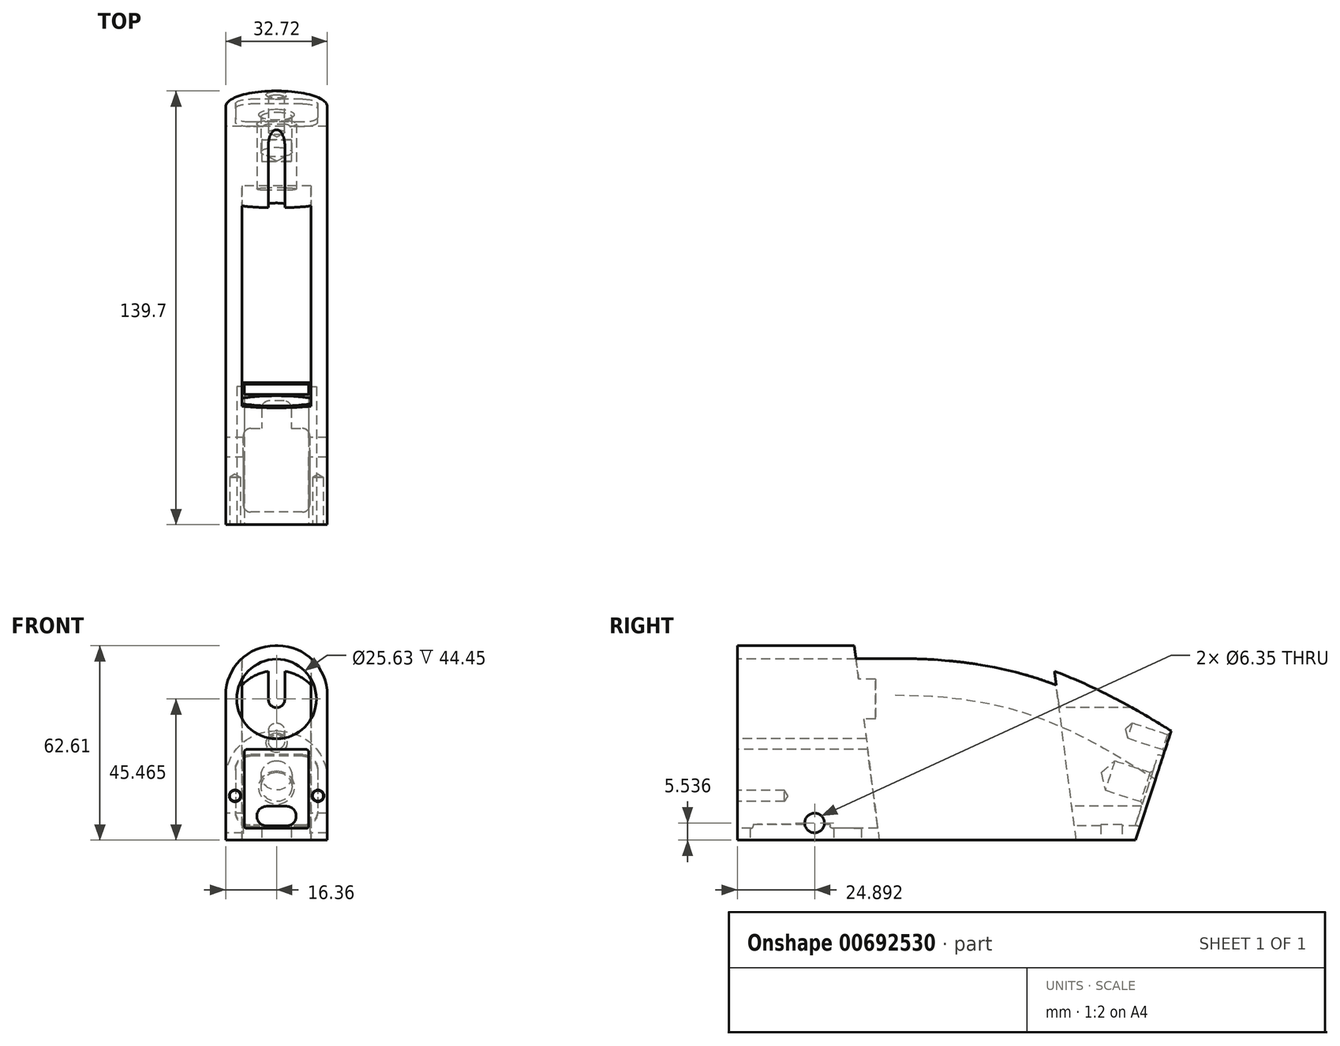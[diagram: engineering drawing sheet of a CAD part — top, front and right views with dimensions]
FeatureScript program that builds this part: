
annotation { "Feature Type Name" : "Feature", "Feature Type Description" : "" }
export const myFeature = defineFeature(function(context is Context, id is Id, definition is map)
    precondition{}
    {
        {
            var Q0;
            Q0=qCreatedBy(makeId("Right.planeOp"),FACE);
            var sketch = newSketch(context, id + "F0", { "sketchPlane" : qUnion([Q0])});
            skLineSegment(sketch, "E0.bottom", {"start": v(0, 0) * mm, "end": v(50.8, 0) * mm});
            skLineSegment(sketch, "E0.top", {"start": v(0, -62.61) * mm, "end": v(128.27, -62.61) * mm});
            skLineSegment(sketch, "E0.left", {"start": v(0, 0) * mm, "end": v(0, -62.61) * mm});
            skCircle(sketch, "E1", {"center": v(24.9, -57.07) * mm, "radius": 3.18 * mm});
            skLineSegment(sketch, "E2", {"start": v(128.27, -62.61) * mm, "end": v(139.7, -27.43) * mm});
            skFitSpline(sketch, "E3", {"points": [v(139.7, -27.43) * mm, v(50.8, 0) * mm], "startDerivative": vector(-81.05, 50.52) * mm, "endDerivative": vector(-120.57, 0) * mm});
            skSolve(sketch);
        }
        {
            var Q0;
            Q0 = qSketchRegion(id + "F0", true);
            extrude(context, id + "F1", {"entities" : qUnion([Q0]), "endBound" : BoundingType.SYMMETRIC, "depth" : 32.72 * mm, "offsetDistance" : 25.4 * mm});
        }
        {
            var Q0;
            Q0=qCreatedBy(makeId("Right.planeOp"),FACE);
            var sketch = newSketch(context, id + "F2", { "sketchPlane" : qUnion([Q0])});
            skLineSegment(sketch, "E4", {"start": v(36.1, 12.1) * mm, "end": v(45.72, -62.61) * mm});
            skLineSegment(sketch, "E5", {"start": v(45.72, -62.61) * mm, "end": v(109.1, -62.61) * mm});
            skLineSegment(sketch, "E6", {"start": v(109.1, -62.61) * mm, "end": v(98.46, 20.11) * mm});
            skLineSegment(sketch, "E7", {"start": v(98.46, 20.11) * mm, "end": v(36.1, 12.1) * mm});
            skSolve(sketch);
        }
        {
            var Q0;
            Q0=makeQuery(id+"F2.imprint","IMPRINT",FACE,{"disambiguationData":[TD([[makeQuery(id+"F2.imprint","IMPRINT",EDGE,{"derivedFrom":sQuery(id+"F2.wireOp",EDGE,"E4")}),1.0]])]});
            extrude(context, id + "F3", {"entities" : qUnion([Q0]), "operationType" : NewBodyOperationType.REMOVE, "endBound" : BoundingType.SYMMETRIC, "depth" : 22.22 * mm, "offsetDistance" : 25.4 * mm});
        }
        {
            var Q0;
            Q0=makeQuery(id+"F1.opExtrude","SWEPT_FACE",FACE,{"disambiguationData":[OSD([sQuery(id+"F0.wireOp",EDGE,"E2")])]});
            var sketch = newSketch(context, id + "F4", { "sketchPlane" : qUnion([Q0])});
            skLineSegment(sketch, "E8.bottom", {"start": v(-8.46, 8.54) * mm, "end": v(8.46, 8.54) * mm});
            skLineSegment(sketch, "E8.top", {"start": v(-8.46, -15.34) * mm, "end": v(8.46, -15.34) * mm});
            skLineSegment(sketch, "E8.left", {"start": v(-13.2, 3.79) * mm, "end": v(-13.2, -10.59) * mm});
            skLineSegment(sketch, "E8.right", {"start": v(13.2, 3.79) * mm, "end": v(13.2, -10.59) * mm});
            skPoint(sketch, "E9.visualSharp", {"position": v(-13.2, 8.54) * mm});
            skArc(sketch, "E9.filletArc", {"start": v(-8.46, 8.54) * mm, "mid": v(-11.82, 7.15) * mm, "end": v(-13.2, 3.79) * mm});
            skPoint(sketch, "E10.visualSharp", {"position": v(13.2, 8.54) * mm});
            skArc(sketch, "E10.filletArc", {"start": v(13.2, 3.79) * mm, "mid": v(11.82, 7.15) * mm, "end": v(8.46, 8.54) * mm});
            skPoint(sketch, "E11.visualSharp", {"position": v(13.2, -15.34) * mm});
            skArc(sketch, "E11.filletArc", {"start": v(8.46, -15.34) * mm, "mid": v(11.82, -13.95) * mm, "end": v(13.2, -10.59) * mm});
            skPoint(sketch, "E12.visualSharp", {"position": v(-13.2, -15.34) * mm});
            skArc(sketch, "E12.filletArc", {"start": v(-13.2, -10.59) * mm, "mid": v(-11.82, -13.95) * mm, "end": v(-8.46, -15.34) * mm});
            skCircle(sketch, "E13", {"center": v(0, -2.64) * mm, "radius": 5.55 * mm});
            skCircle(sketch, "E14", {"center": v(0, 13.11) * mm, "radius": 3.18 * mm});
            skSolve(sketch);
        }
        {
            var Q0;
            Q0=makeQuery(id+"F4.imprint","IMPRINT",FACE,{"disambiguationData":[TD([[makeQuery(id+"F4.imprint","IMPRINT",EDGE,{"derivedFrom":sQuery(id+"F4.wireOp",EDGE,"E8.bottom")}),-1.0]])]});
            extrude(context, id + "F5", {"entities" : qUnion([Q0]), "operationType" : NewBodyOperationType.REMOVE, "oppositeDirection" : true, "depth" : 1.6 * mm, "offsetDistance" : 25.4 * mm});
        }
        {
            var Q0;
            Q0=sQuery(id+"F4.wireOp",VERTEX,"E14.center");
            var Q1;
            Q1=makeQuery(id+"F1.opExtrude","SWEPT_BODY",BODY,{"disambiguationData":[OSD([sQuery(id+"F0.wireOp",EDGE,"E0.bottom"),sQuery(id+"F0.wireOp",EDGE,"E0.top"),sQuery(id+"F0.wireOp",EDGE,"E0.left"),sQuery(id+"F0.wireOp",EDGE,"E1"),sQuery(id+"F0.wireOp",EDGE,"E2"),sQuery(id+"F0.wireOp",EDGE,"E3")])]});
            hole(context, id + "F6", {"style" : HoleStyle.C_SINK, "endStyle" : HoleEndStyle.BLIND, "holeDiameter" : 5.1 * mm, "cSinkDiameter" : 6.73 * mm, "cSinkAngle" : 90 * degree, "majorDiameter" : 6.35 * mm, "holeDepth" : 12.7 * mm, "isTappedThrough" : true, "tappedDepth" : 12.7 * mm, "tapClearance" : 3, "locations" : qUnion([Q0]), "scope" : qUnion([Q1])});
        }
        {
            var Q0;
            Q0=sQuery(id+"F4.wireOp",VERTEX,"E13.center");
            var Q1;
            Q1=makeQuery(id+"F1.opExtrude","SWEPT_BODY",BODY,{"disambiguationData":[OSD([sQuery(id+"F0.wireOp",EDGE,"E0.bottom"),sQuery(id+"F0.wireOp",EDGE,"E0.top"),sQuery(id+"F0.wireOp",EDGE,"E0.left"),sQuery(id+"F0.wireOp",EDGE,"E1"),sQuery(id+"F0.wireOp",EDGE,"E2"),sQuery(id+"F0.wireOp",EDGE,"E3")])]});
            hole(context, id + "F7", {"style" : HoleStyle.C_SINK, "endStyle" : HoleEndStyle.BLIND, "holeDiameter" : 9.92 * mm, "cSinkDiameter" : 11.43 * mm, "cSinkAngle" : 90 * degree, "majorDiameter" : 6.35 * mm, "holeDepth" : 12.7 * mm, "isTappedThrough" : true, "tappedDepth" : 12.7 * mm, "tapClearance" : 3, "locations" : qUnion([Q0]), "scope" : qUnion([Q1])});
        }
        {
            var Q0;
            Q0=qCreatedBy(makeId("Front.planeOp"),FACE);
            var sketch = newSketch(context, id + "F8", { "sketchPlane" : qUnion([Q0])});
            skLineSegment(sketch, "E15.bottom", {"start": v(3.17, -58.04) * mm, "end": v(-3.17, -58.04) * mm});
            skLineSegment(sketch, "E15.top", {"start": v(3.17, -51.69) * mm, "end": v(-3.18, -51.69) * mm});
            skLineSegment(sketch, "E15.left", {"start": v(6.35, -54.86) * mm, "end": v(6.35, -54.86) * mm});
            skLineSegment(sketch, "E15.right", {"start": v(-6.35, -54.86) * mm, "end": v(-6.35, -54.86) * mm});
            skPoint(sketch, "E15.middle", {"position": v(0, -54.86) * mm});
            skPoint(sketch, "E16.visualSharp", {"position": v(-6.35, -51.69) * mm});
            skArc(sketch, "E16.filletArc", {"start": v(-3.18, -51.69) * mm, "mid": v(-5.42, -52.62) * mm, "end": v(-6.35, -54.86) * mm});
            skPoint(sketch, "E17.visualSharp", {"position": v(6.35, -51.69) * mm});
            skArc(sketch, "E17.filletArc", {"start": v(6.35, -54.86) * mm, "mid": v(5.42, -52.62) * mm, "end": v(3.17, -51.69) * mm});
            skPoint(sketch, "E18.visualSharp", {"position": v(6.35, -58.04) * mm});
            skArc(sketch, "E18.filletArc", {"start": v(3.17, -58.04) * mm, "mid": v(5.42, -57.1) * mm, "end": v(6.35, -54.86) * mm});
            skPoint(sketch, "E19.visualSharp", {"position": v(-6.35, -58.04) * mm});
            skArc(sketch, "E19.filletArc", {"start": v(-6.35, -54.86) * mm, "mid": v(-5.42, -57.1) * mm, "end": v(-3.17, -58.04) * mm});
            skSolve(sketch);
        }
        {
            var Q0;
            Q0=makeQuery(id+"F8.imprint","IMPRINT",FACE,{"disambiguationData":[TD([[makeQuery(id+"F8.imprint","IMPRINT",EDGE,{"derivedFrom":sQuery(id+"F8.wireOp",EDGE,"E15.bottom")}),-1.0]])]});
            extrude(context, id + "F9", {"entities" : qUnion([Q0]), "operationType" : NewBodyOperationType.REMOVE, "endBound" : BoundingType.THROUGH_ALL, "oppositeDirection" : true, "depth" : 25.4 * mm, "offsetDistance" : 25.4 * mm});
        }
        {
            var Q0;
            Q0=qCreatedBy(makeId("Front.planeOp"),FACE);
            var sketch = newSketch(context, id + "F10", { "sketchPlane" : qUnion([Q0])});
            skLineSegment(sketch, "E20.bottom", {"start": v(-9.59, -58.8) * mm, "end": v(9.59, -58.8) * mm});
            skLineSegment(sketch, "E20.top", {"start": v(-9.59, -33.4) * mm, "end": v(9.59, -33.4) * mm});
            skLineSegment(sketch, "E20.left", {"start": v(-10.35, -58.04) * mm, "end": v(-10.35, -34.16) * mm});
            skLineSegment(sketch, "E20.right", {"start": v(10.35, -58.04) * mm, "end": v(10.35, -34.16) * mm});
            skPoint(sketch, "E20.middle", {"position": v(0, -46.1) * mm});
            skPoint(sketch, "E21.visualSharp", {"position": v(-10.35, -33.4) * mm});
            skArc(sketch, "E21.filletArc", {"start": v(-9.59, -33.4) * mm, "mid": v(-10.13, -33.62) * mm, "end": v(-10.35, -34.16) * mm});
            skPoint(sketch, "E22.visualSharp", {"position": v(10.35, -33.4) * mm});
            skArc(sketch, "E22.filletArc", {"start": v(10.35, -34.16) * mm, "mid": v(10.13, -33.62) * mm, "end": v(9.59, -33.4) * mm});
            skPoint(sketch, "E23.visualSharp", {"position": v(10.35, -58.8) * mm});
            skArc(sketch, "E23.filletArc", {"start": v(9.59, -58.8) * mm, "mid": v(10.13, -58.58) * mm, "end": v(10.35, -58.04) * mm});
            skPoint(sketch, "E24.visualSharp", {"position": v(-10.35, -58.8) * mm});
            skArc(sketch, "E24.filletArc", {"start": v(-10.35, -58.04) * mm, "mid": v(-10.13, -58.58) * mm, "end": v(-9.59, -58.8) * mm});
            skSolve(sketch);
        }
        {
            var Q0;
            Q0 = qSketchRegion(id + "F10", true);
            extrude(context, id + "F11", {"entities" : qUnion([Q0]), "operationType" : NewBodyOperationType.REMOVE, "endBound" : BoundingType.UP_TO_NEXT, "oppositeDirection" : true, "depth" : 25.4 * mm, "offsetDistance" : 25.4 * mm});
        }
        {
            var Q0;
            Q0=qCreatedBy(makeId("Front.planeOp"),FACE);
            var sketch = newSketch(context, id + "F12", { "sketchPlane" : qUnion([Q0])});
            skCircle(sketch, "E25", {"center": v(-13.36, -48.34) * mm, "radius": 1.73 * mm});
            skCircle(sketch, "E26", {"center": v(13.36, -48.34) * mm, "radius": 1.73 * mm});
            skSolve(sketch);
        }
        {
            var Q0;
            Q0=sQuery(id+"F12.wireOp",VERTEX,"E25.center");
            var Q1;
            Q1=sQuery(id+"F12.wireOp",VERTEX,"E26.center");
            var Q2;
            Q2=makeQuery(id+"F1.opExtrude","SWEPT_BODY",BODY,{"disambiguationData":[OSD([sQuery(id+"F0.wireOp",EDGE,"E0.bottom"),sQuery(id+"F0.wireOp",EDGE,"E0.top"),sQuery(id+"F0.wireOp",EDGE,"E0.left"),sQuery(id+"F0.wireOp",EDGE,"E1"),sQuery(id+"F0.wireOp",EDGE,"E2"),sQuery(id+"F0.wireOp",EDGE,"E3")])]});
            hole(context, id + "F13", {"style" : HoleStyle.C_SINK, "endStyle" : HoleEndStyle.BLIND, "holeDiameter" : 3.45 * mm, "cSinkDiameter" : 3.8 * mm, "cSinkAngle" : 90 * degree, "majorDiameter" : 6.35 * mm, "holeDepth" : 15.24 * mm, "isTappedThrough" : true, "tappedDepth" : 12.7 * mm, "tapClearance" : 3, "locations" : qUnion([Q0, Q1]), "scope" : qUnion([Q2])});
        }
        {
            var Q0;
            Q0=qCreatedBy(makeId("Front.planeOp"),FACE);
            var sketch = newSketch(context, id + "F14", { "sketchPlane" : qUnion([Q0])});
            skCircle(sketch, "E27", {"center": v(0, -17.14) * mm, "radius": 12.81 * mm});
            skSolve(sketch);
        }
        {
            var Q0;
            Q0=makeQuery(id+"F14.imprint","IMPRINT",FACE,{"disambiguationData":[TD([[makeQuery(id+"F14.imprint","IMPRINT",EDGE,{"derivedFrom":sQuery(id+"F14.wireOp",EDGE,"E27")}),1.0]])]});
            extrude(context, id + "F15", {"entities" : qUnion([Q0]), "operationType" : NewBodyOperationType.REMOVE, "oppositeDirection" : true, "depth" : 44.45 * mm, "offsetDistance" : 25.4 * mm});
        }
        {
            var Q0;
            Q0=makeQuery(id+"F1.opExtrude","SWEPT_FACE",FACE,{"disambiguationData":[OSD([sQuery(id+"F0.wireOp",EDGE,"E0.top")])]});
            var sketch = newSketch(context, id + "F16", { "sketchPlane" : qUnion([Q0])});
            skLineSegment(sketch, "E28.bottom", {"start": v(4.76, -123.95) * mm, "end": v(-4.76, -123.95) * mm});
            skLineSegment(sketch, "E28.top", {"start": v(4.76, -116.97) * mm, "end": v(-4.76, -116.97) * mm});
            skLineSegment(sketch, "E28.left", {"start": v(4.76, -123.95) * mm, "end": v(4.76, -116.97) * mm});
            skLineSegment(sketch, "E28.right", {"start": v(-4.76, -123.95) * mm, "end": v(-4.76, -116.97) * mm});
            skPoint(sketch, "E28.middle", {"position": v(0, -120.46) * mm});
            skLineSegment(sketch, "E29.top", {"start": v(8.34, -4.06) * mm, "end": v(-8.34, -4.06) * mm});
            skLineSegment(sketch, "E29.left", {"start": v(10.7, -28.63) * mm, "end": v(10.7, -6.43) * mm});
            skLineSegment(sketch, "E29.right", {"start": v(-10.7, -28.63) * mm, "end": v(-10.7, -6.43) * mm});
            skPoint(sketch, "E29.middle", {"position": v(0, -17.53) * mm});
            skLineSegment(sketch, "E30.bottom", {"start": v(2.44, -39.88) * mm, "end": v(-2.44, -39.88) * mm});
            skLineSegment(sketch, "E30.left", {"start": v(4.8, -37.52) * mm, "end": v(4.8, -30.99) * mm});
            skLineSegment(sketch, "E30.right", {"start": v(-4.8, -37.52) * mm, "end": v(-4.8, -30.99) * mm});
            skPoint(sketch, "E30.middle", {"position": v(0, -30.72) * mm});
            skPoint(sketch, "E31.visualSharp", {"position": v(-10.7, -4.06) * mm});
            skArc(sketch, "E31.filletArc", {"start": v(-8.34, -4.06) * mm, "mid": v(-10.01, -4.76) * mm, "end": v(-10.7, -6.43) * mm});
            skPoint(sketch, "E32.visualSharp", {"position": v(10.7, -4.06) * mm});
            skArc(sketch, "E32.filletArc", {"start": v(10.7, -6.43) * mm, "mid": v(10.01, -4.76) * mm, "end": v(8.34, -4.06) * mm});
            skPoint(sketch, "E33.visualSharp", {"position": v(10.7, -30.99) * mm});
            skArc(sketch, "E33.filletArc", {"start": v(8.34, -30.99) * mm, "mid": v(10.01, -30.3) * mm, "end": v(10.7, -28.63) * mm});
            skPoint(sketch, "E34.visualSharp", {"position": v(-10.7, -30.99) * mm});
            skArc(sketch, "E34.filletArc", {"start": v(-10.7, -28.63) * mm, "mid": v(-10.01, -30.3) * mm, "end": v(-8.34, -30.99) * mm});
            skPoint(sketch, "E35.visualSharp", {"position": v(-4.8, -39.88) * mm});
            skArc(sketch, "E35.filletArc", {"start": v(-4.8, -37.52) * mm, "mid": v(-4.1, -39.19) * mm, "end": v(-2.44, -39.88) * mm});
            skPoint(sketch, "E36.visualSharp", {"position": v(4.8, -39.88) * mm});
            skArc(sketch, "E36.filletArc", {"start": v(2.44, -39.88) * mm, "mid": v(4.1, -39.19) * mm, "end": v(4.8, -37.52) * mm});
            skLineSegment(sketch, "E37", {"start": v(-8.34, -30.99) * mm, "end": v(-4.8, -30.99) * mm});
            skLineSegment(sketch, "E38", {"start": v(4.8, -30.99) * mm, "end": v(8.34, -30.99) * mm});
            skSolve(sketch);
        }
        {
            var Q0;
            Q0=makeQuery(id+"F16.imprint","IMPRINT",FACE,{"disambiguationData":[TD([[makeQuery(id+"F16.imprint","IMPRINT",EDGE,{"derivedFrom":sQuery(id+"F16.wireOp",EDGE,"E29.top")}),1.0]])]});
            var Q1;
            Q1=makeQuery(id+"F16.imprint","IMPRINT",FACE,{"disambiguationData":[TD([[makeQuery(id+"F16.imprint","IMPRINT",EDGE,{"derivedFrom":sQuery(id+"F16.wireOp",EDGE,"E28.bottom")}),-1.0]])]});
            extrude(context, id + "F17", {"entities" : qUnion([Q0, Q1]), "operationType" : NewBodyOperationType.REMOVE, "oppositeDirection" : true, "depth" : 5.08 * mm, "offsetDistance" : 25.4 * mm});
        }
        {
            var Q0;
            Q0=makeQuery(id+"F1.opExtrude","CAP_EDGE",EDGE,{"disambiguationData":[OSD([sQuery(id+"F0.wireOp",EDGE,"E0.bottom")])],"isStart":false});
            var Q1;
            Q1=makeQuery(id+"F1.opExtrude","CAP_EDGE",EDGE,{"disambiguationData":[OSD([sQuery(id+"F0.wireOp",EDGE,"E0.bottom")])],"isStart":true});
            fillet(context, id + "F18", {"entities" : qUnion([Q0, Q1]), "radius" : 15.88 * mm, "tangentPropagation" : true, "allowEdgeOverflow" : false});
        }
        {
            var Q0;
            Q0=qCreatedBy(makeId("Front.planeOp"),FACE);
            var sketch = newSketch(context, id + "F19", { "sketchPlane" : qUnion([Q0])});
            skArc(sketch, "E39", {"start": v(-2.67, -17.27) * mm, "mid": v(0, -19.94) * mm, "end": v(2.67, -17.27) * mm});
            skLineSegment(sketch, "E40", {"start": v(-2.67, -17.27) * mm, "end": v(-2.67, -6.04) * mm});
            skLineSegment(sketch, "E41", {"start": v(2.67, -17.27) * mm, "end": v(2.67, -6.04) * mm});
            skLineSegment(sketch, "E42", {"start": v(-2.67, -6.04) * mm, "end": v(2.67, -6.04) * mm});
            skSolve(sketch);
        }
        {
            var Q0;
            Q0 = qSketchRegion(id + "F19", true);
            extrude(context, id + "F20", {"entities" : qUnion([Q0]), "operationType" : NewBodyOperationType.REMOVE, "endBound" : BoundingType.THROUGH_ALL, "oppositeDirection" : true, "depth" : 25.4 * mm, "offsetDistance" : 25.4 * mm});
        }
    });
